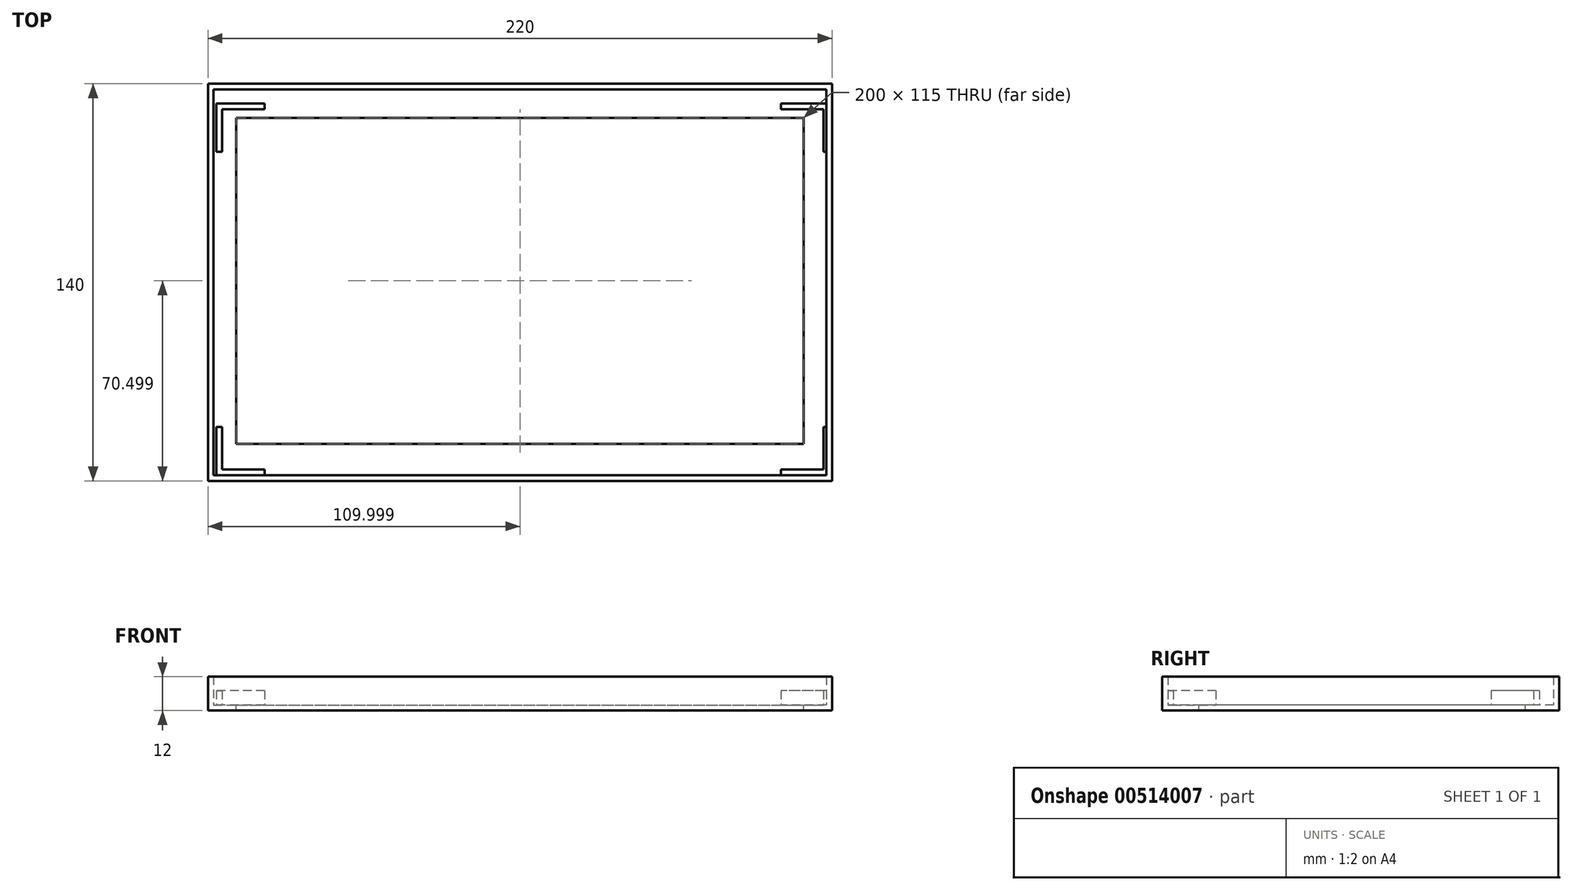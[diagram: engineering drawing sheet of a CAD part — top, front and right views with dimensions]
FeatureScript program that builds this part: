
annotation { "Feature Type Name" : "Feature", "Feature Type Description" : "" }
export const myFeature = defineFeature(function(context is Context, id is Id, definition is map)
    precondition{}
    {
        {
            var Q0;
            Q0=qCreatedBy(makeId("Top.planeOp"),FACE);
            var sketch = newSketch(context, id + "F0", { "sketchPlane" : qUnion([Q0])});
            skLineSegment(sketch, "E0.bottom", {"start": v(-111.94, 78.48) * mm, "end": v(108.06, 78.48) * mm});
            skLineSegment(sketch, "E0.top", {"start": v(-111.94, -61.52) * mm, "end": v(108.06, -61.52) * mm});
            skLineSegment(sketch, "E0.left", {"start": v(-111.94, 78.48) * mm, "end": v(-111.94, -61.52) * mm});
            skLineSegment(sketch, "E0.right", {"start": v(108.06, 78.48) * mm, "end": v(108.06, -61.52) * mm});
            skLineSegment(sketch, "E1.bottom", {"start": v(-101.94, 66.48) * mm, "end": v(98.06, 66.48) * mm});
            skLineSegment(sketch, "E1.top", {"start": v(-101.94, -48.52) * mm, "end": v(98.06, -48.52) * mm});
            skLineSegment(sketch, "E1.left", {"start": v(-101.94, 66.48) * mm, "end": v(-101.94, -48.52) * mm});
            skLineSegment(sketch, "E1.right", {"start": v(98.06, 66.48) * mm, "end": v(98.06, -48.52) * mm});
            skLineSegment(sketch, "E2.top", {"start": v(-108.94, 54.48) * mm, "end": v(-106.94, 54.48) * mm});
            skLineSegment(sketch, "E2.left", {"start": v(-108.94, 69.48) * mm, "end": v(-108.94, 54.48) * mm});
            skLineSegment(sketch, "E2.right", {"start": v(-106.94, 69.48) * mm, "end": v(-106.94, 54.48) * mm});
            skLineSegment(sketch, "E3.bottom", {"start": v(-91.94, 71.48) * mm, "end": v(-91.94, 69.48) * mm});
            skLineSegment(sketch, "E3.left", {"start": v(-91.94, 71.48) * mm, "end": v(-106.94, 71.48) * mm});
            skLineSegment(sketch, "E3.right", {"start": v(-91.94, 69.48) * mm, "end": v(-106.94, 69.48) * mm});
            skLineSegment(sketch, "E4", {"start": v(-106.94, 71.48) * mm, "end": v(-108.94, 71.48) * mm});
            skLineSegment(sketch, "E5", {"start": v(-108.94, 71.48) * mm, "end": v(-108.94, 69.48) * mm});
            skLineSegment(sketch, "E6.top", {"start": v(90.06, 71.48) * mm, "end": v(90.06, 69.48) * mm});
            skLineSegment(sketch, "E6.left", {"start": v(105.06, 71.48) * mm, "end": v(90.06, 71.48) * mm});
            skLineSegment(sketch, "E6.right", {"start": v(105.06, 69.48) * mm, "end": v(90.06, 69.48) * mm});
            skLineSegment(sketch, "E7.bottom", {"start": v(107.06, 54.48) * mm, "end": v(105.06, 54.48) * mm});
            skLineSegment(sketch, "E7.left", {"start": v(107.06, 54.48) * mm, "end": v(107.06, 69.48) * mm});
            skLineSegment(sketch, "E7.right", {"start": v(105.06, 54.48) * mm, "end": v(105.06, 69.48) * mm});
            skLineSegment(sketch, "E8", {"start": v(107.06, 69.48) * mm, "end": v(107.06, 71.48) * mm});
            skLineSegment(sketch, "E9", {"start": v(107.06, 71.48) * mm, "end": v(105.06, 71.48) * mm});
            skLineSegment(sketch, "E10.top", {"start": v(-91.94, -59.52) * mm, "end": v(-91.94, -57.52) * mm});
            skLineSegment(sketch, "E10.left", {"start": v(-106.94, -59.52) * mm, "end": v(-91.94, -59.52) * mm});
            skLineSegment(sketch, "E10.right", {"start": v(-106.94, -57.52) * mm, "end": v(-91.94, -57.52) * mm});
            skLineSegment(sketch, "E11.bottom", {"start": v(-108.94, -42.52) * mm, "end": v(-106.94, -42.52) * mm});
            skLineSegment(sketch, "E11.left", {"start": v(-108.94, -42.52) * mm, "end": v(-108.94, -57.52) * mm});
            skLineSegment(sketch, "E11.right", {"start": v(-106.94, -42.52) * mm, "end": v(-106.94, -57.52) * mm});
            skLineSegment(sketch, "E12", {"start": v(-108.94, -57.52) * mm, "end": v(-108.94, -59.52) * mm});
            skLineSegment(sketch, "E13", {"start": v(-108.94, -59.52) * mm, "end": v(-106.94, -59.52) * mm});
            skLineSegment(sketch, "E14.top", {"start": v(107.06, -42.52) * mm, "end": v(105.06, -42.52) * mm});
            skLineSegment(sketch, "E14.left", {"start": v(107.06, -57.52) * mm, "end": v(107.06, -42.52) * mm});
            skLineSegment(sketch, "E14.right", {"start": v(105.06, -57.52) * mm, "end": v(105.06, -42.52) * mm});
            skLineSegment(sketch, "E15.bottom", {"start": v(90.06, -59.52) * mm, "end": v(90.06, -57.52) * mm});
            skLineSegment(sketch, "E15.left", {"start": v(90.06, -59.52) * mm, "end": v(105.06, -59.52) * mm});
            skLineSegment(sketch, "E15.right", {"start": v(90.06, -57.52) * mm, "end": v(105.06, -57.52) * mm});
            skLineSegment(sketch, "E16", {"start": v(105.06, -59.52) * mm, "end": v(107.06, -59.52) * mm});
            skLineSegment(sketch, "E17", {"start": v(107.06, -59.52) * mm, "end": v(107.06, -57.52) * mm});
            skLineSegment(sketch, "E18.bottom", {"start": v(-109.94, 76.48) * mm, "end": v(106.06, 76.48) * mm});
            skLineSegment(sketch, "E18.top", {"start": v(-109.94, -59.52) * mm, "end": v(106.06, -59.52) * mm});
            skLineSegment(sketch, "E18.left", {"start": v(-109.94, 76.48) * mm, "end": v(-109.94, -59.52) * mm});
            skLineSegment(sketch, "E18.right", {"start": v(106.06, 76.48) * mm, "end": v(106.06, -59.52) * mm});
            skSolve(sketch);
        }
        {
            var Q0;
            Q0=makeQuery(id+"F0.imprint","IMPRINT",FACE,{"disambiguationData":[TD([[makeQuery(id+"F0.imprint","IMPRINT",EDGE,{"derivedFrom":sQuery(id+"F0.wireOp",EDGE,"E1.bottom")}),1.0]])]});
            var Q1;
            {var subQ0=sQuery(id+"F0.wireOp",EDGE,"E10.top");Q1=makeQuery(id+"F0.imprint","IMPRINT",FACE,{"disambiguationData":[TD([[makeQuery(id+"F0.imprint","IMPRINT",EDGE,{"derivedFrom":subQ0}),1.0]])]});}
            var Q2;
            Q2=makeQuery(id+"F0.imprint","IMPRINT",FACE,{"disambiguationData":[TD([[makeQuery(id+"F0.imprint","IMPRINT",EDGE,{"derivedFrom":sQuery(id+"F0.wireOp",EDGE,"E2.top")}),1.0]])]});
            var Q3;
            Q3=makeQuery(id+"F0.imprint","IMPRINT",FACE,{"disambiguationData":[TD([[makeQuery(id+"F0.imprint","IMPRINT",EDGE,{"derivedFrom":sQuery(id+"F0.wireOp",EDGE,"E6.top")}),1.0]])]});
            var Q4;
            {var subQ1=sQuery(id+"F0.wireOp",EDGE,"E7.left");Q4=makeQuery(id+"F0.imprint","IMPRINT",FACE,{"disambiguationData":[TD([[makeQuery(id+"F0.imprint","IMPRINT",EDGE,{"derivedFrom":subQ1}),1.0]])]});}
            var Q5;
            {var subQ1=sQuery(id+"F0.wireOp",EDGE,"E14.right");Q5=makeQuery(id+"F0.imprint","IMPRINT",FACE,{"disambiguationData":[TD([[makeQuery(id+"F0.imprint","IMPRINT",EDGE,{"derivedFrom":subQ1}),-1.0]])]});}
            var Q6;
            Q6=makeQuery(id+"F0.imprint","IMPRINT",FACE,{"disambiguationData":[TD([[makeQuery(id+"F0.imprint","IMPRINT",EDGE,{"derivedFrom":sQuery(id+"F0.wireOp",EDGE,"E0.bottom")}),-1.0]])]});
            var Q7;
            {var subQ4=sQuery(id+"F0.wireOp",EDGE,"E14.left");Q7=makeQuery(id+"F0.imprint","IMPRINT",FACE,{"disambiguationData":[TD([[makeQuery(id+"F0.imprint","IMPRINT",EDGE,{"derivedFrom":subQ4}),1.0]])]});}
            extrude(context, id + "F1", {"entities" : qUnion([Q0, Q1, Q2, Q3, Q4, Q5, Q6, Q7]), "oppositeDirection" : true, "depth" : 2 * mm});
        }
        {
            var Q0;
            Q0=makeQuery(id+"F0.imprint","IMPRINT",FACE,{"disambiguationData":[TD([[makeQuery(id+"F0.imprint","IMPRINT",EDGE,{"derivedFrom":sQuery(id+"F0.wireOp",EDGE,"E2.top")}),1.0]])]});
            var Q1;
            Q1=makeQuery(id+"F0.imprint","IMPRINT",FACE,{"disambiguationData":[TD([[makeQuery(id+"F0.imprint","IMPRINT",EDGE,{"derivedFrom":sQuery(id+"F0.wireOp",EDGE,"E10.top")}),1.0]])]});
            var Q2;
            Q2=makeQuery(id+"F0.imprint","IMPRINT",FACE,{"disambiguationData":[TD([[makeQuery(id+"F0.imprint","IMPRINT",EDGE,{"derivedFrom":sQuery(id+"F0.wireOp",EDGE,"E6.top")}),1.0]])]});
            var Q3;
            {var subQ1=sQuery(id+"F0.wireOp",EDGE,"E14.right");Q3=makeQuery(id+"F0.imprint","IMPRINT",FACE,{"disambiguationData":[TD([[makeQuery(id+"F0.imprint","IMPRINT",EDGE,{"derivedFrom":subQ1}),-1.0]])]});}
            extrude(context, id + "F2", {"entities" : qUnion([Q0, Q1, Q2, Q3]), "operationType" : NewBodyOperationType.ADD, "depth" : 5 * mm});
        }
        {
            var Q0;
            Q0=makeQuery(id+"F0.imprint","IMPRINT",FACE,{"disambiguationData":[TD([[makeQuery(id+"F0.imprint","IMPRINT",EDGE,{"derivedFrom":sQuery(id+"F0.wireOp",EDGE,"E0.bottom")}),-1.0]])]});
            var Q1;
            {var subQ4=sQuery(id+"F0.wireOp",EDGE,"E14.left");Q1=makeQuery(id+"F0.imprint","IMPRINT",FACE,{"disambiguationData":[TD([[makeQuery(id+"F0.imprint","IMPRINT",EDGE,{"derivedFrom":subQ4}),1.0]])]});}
            var Q2;
            {var subQ1=sQuery(id+"F0.wireOp",EDGE,"E7.left");Q2=makeQuery(id+"F0.imprint","IMPRINT",FACE,{"disambiguationData":[TD([[makeQuery(id+"F0.imprint","IMPRINT",EDGE,{"derivedFrom":subQ1}),1.0]])]});}
            extrude(context, id + "F3", {"entities" : qUnion([Q0, Q1, Q2]), "operationType" : NewBodyOperationType.ADD, "depth" : 10 * mm});
        }
    });
